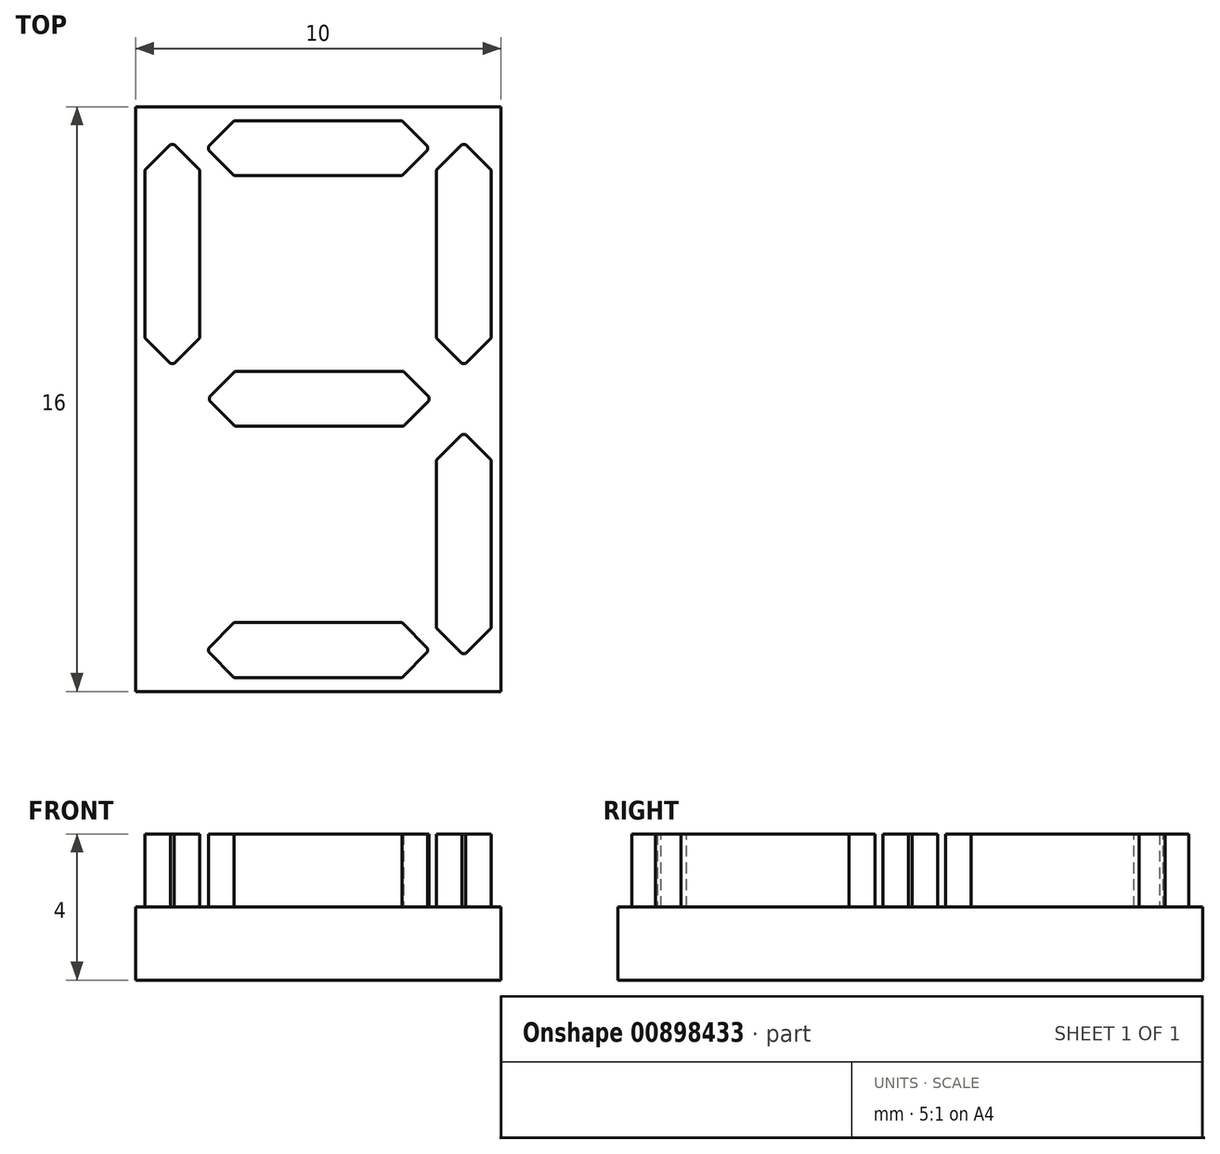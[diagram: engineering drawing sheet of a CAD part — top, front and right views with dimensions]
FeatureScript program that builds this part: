
annotation { "Feature Type Name" : "Feature", "Feature Type Description" : "" }
export const myFeature = defineFeature(function(context is Context, id is Id, definition is map)
    precondition{}
    {
        {
            var Q0;
            Q0=qCreatedBy(makeId("Top.planeOp"),FACE);
            var sketch = newSketch(context, id + "F0", { "sketchPlane" : qUnion([Q0])});
            skLineSegment(sketch, "E0.bottom", {"start": v(5, -8) * mm, "end": v(-5, -8) * mm});
            skLineSegment(sketch, "E0.top", {"start": v(5, 8) * mm, "end": v(-5, 8) * mm});
            skLineSegment(sketch, "E0.left", {"start": v(5, -8) * mm, "end": v(5, 8) * mm});
            skLineSegment(sketch, "E0.right", {"start": v(-5, -8) * mm, "end": v(-5, 8) * mm});
            skPoint(sketch, "E0.middle", {"position": v(0, 0) * mm});
            skSolve(sketch);
        }
        {
            var Q0;
            Q0=qSketchRegion(id+"F0",true);
            extrude(context, id + "F1", {"entities" : qUnion([Q0]), "oppositeDirection" : true, "depth" : 2 * mm, "offsetDistance" : 25 * mm});
        }
        {
            var Q0;
            Q0=makeQuery(id+"F1.opExtrude","CAP_FACE",FACE,{"disambiguationData":[OSD([sQuery(id+"F0.wireOp",EDGE,"E0.bottom"),sQuery(id+"F0.wireOp",EDGE,"E0.top"),sQuery(id+"F0.wireOp",EDGE,"E0.left"),sQuery(id+"F0.wireOp",EDGE,"E0.right")])],"isStart":true});
            var sketch = newSketch(context, id + "F2", { "sketchPlane" : qUnion([Q0])});
            skLineSegment(sketch, "E1", {"start": v(0, 8) * mm, "end": v(0, -8) * mm, "construction": true});
            skLineSegment(sketch, "E2", {"start": v(-5, 0) * mm, "end": v(5, 0) * mm, "construction": true});
            skLineSegment(sketch, "E3.bottom", {"start": v(3, 6.12) * mm, "end": v(-3, 6.12) * mm});
            skLineSegment(sketch, "E3.top", {"start": v(3, 7.62) * mm, "end": v(-3, 7.62) * mm});
            skLineSegment(sketch, "E3.left", {"start": v(3, 6.12) * mm, "end": v(3, 7.62) * mm});
            skLineSegment(sketch, "E3.right", {"start": v(-3, 6.12) * mm, "end": v(-3, 7.62) * mm});
            skPoint(sketch, "E3.middle", {"position": v(0, 6.87) * mm});
            skLineSegment(sketch, "E4.MirrorCS", {"start": v(-3, -6.12) * mm, "end": v(-3, -7.62) * mm});
            skLineSegment(sketch, "E5.MirrorCS", {"start": v(3, -6.12) * mm, "end": v(3, -7.62) * mm});
            skPoint(sketch, "E6.MirrorP", {"position": v(0, -6.87) * mm});
            skLineSegment(sketch, "E7.MirrorCS", {"start": v(3, -6.12) * mm, "end": v(-3, -6.12) * mm});
            skLineSegment(sketch, "E8.MirrorCS", {"start": v(4.74, -6.97) * mm, "end": v(4.74, -0.97) * mm});
            skLineSegment(sketch, "E9.MirrorCS", {"start": v(3, -7.62) * mm, "end": v(-3, -7.62) * mm});
            skLineSegment(sketch, "E10.MirrorCS", {"start": v(3.24, -6.97) * mm, "end": v(3.24, -0.47) * mm});
            skLineSegment(sketch, "E11.MirrorCS", {"start": v(3.24, -0.97) * mm, "end": v(4.74, -0.97) * mm});
            skLineSegment(sketch, "E12.MirrorCS", {"start": v(3.24, -6.97) * mm, "end": v(4.74, -6.97) * mm});
            skPoint(sketch, "E13.middle", {"position": v(0, 0) * mm});
            skLineSegment(sketch, "E14.MirrorCS", {"start": v(-3.24, 0.97) * mm, "end": v(-4.74, 0.97) * mm});
            skLineSegment(sketch, "E15.MirrorCS", {"start": v(4.74, 6.97) * mm, "end": v(4.74, 0.97) * mm});
            skLineSegment(sketch, "E16.MirrorCS", {"start": v(3.24, 0.97) * mm, "end": v(4.74, 0.97) * mm});
            skLineSegment(sketch, "E17.MirrorCS", {"start": v(3.24, 6.97) * mm, "end": v(4.74, 6.97) * mm});
            skLineSegment(sketch, "E18.MirrorCS", {"start": v(-4.74, 6.97) * mm, "end": v(-4.74, 0.97) * mm});
            skLineSegment(sketch, "E19.MirrorCS", {"start": v(3.24, 6.97) * mm, "end": v(3.24, 0.47) * mm});
            skLineSegment(sketch, "E20.MirrorCS", {"start": v(-3.24, 6.97) * mm, "end": v(-3.24, 0.47) * mm});
            skLineSegment(sketch, "E21.MirrorCS", {"start": v(-3.24, 6.97) * mm, "end": v(-4.74, 6.97) * mm});
            skLineSegment(sketch, "E22.MirrorCS", {"start": v(-2.97, 0.76) * mm, "end": v(-2.97, -0.74) * mm});
            skLineSegment(sketch, "E23.MirrorCS", {"start": v(3.03, 0.76) * mm, "end": v(3.03, -0.74) * mm});
            skLineSegment(sketch, "E24.MirrorCS", {"start": v(3.03, 0.76) * mm, "end": v(-2.97, 0.76) * mm});
            skLineSegment(sketch, "E25.MirrorCS", {"start": v(3.03, -0.74) * mm, "end": v(-2.97, -0.74) * mm});
            skSolve(sketch);
        }
        {
            var Q0;
            Q0=makeQuery(id+"F2.imprint","IMPRINT",FACE,{"disambiguationData":[TD([[makeQuery(id+"F2.imprint","IMPRINT",EDGE,{"derivedFrom":sQuery(id+"F2.wireOp",EDGE,"E14.MirrorCS")}),-1.0]])]});
            var Q1;
            Q1=makeQuery(id+"F2.imprint","IMPRINT",FACE,{"disambiguationData":[TD([[makeQuery(id+"F2.imprint","IMPRINT",EDGE,{"derivedFrom":sQuery(id+"F2.wireOp",EDGE,"E3.top")}),1.0]])]});
            var Q2;
            Q2=makeQuery(id+"F2.imprint","IMPRINT",FACE,{"disambiguationData":[TD([[makeQuery(id+"F2.imprint","IMPRINT",EDGE,{"derivedFrom":sQuery(id+"F2.wireOp",EDGE,"E15.MirrorCS")}),-1.0]])]});
            var Q3;
            Q3=makeQuery(id+"F2.imprint","IMPRINT",FACE,{"disambiguationData":[TD([[makeQuery(id+"F2.imprint","IMPRINT",EDGE,{"derivedFrom":sQuery(id+"F2.wireOp",EDGE,"E22.MirrorCS")}),1.0]])]});
            var Q4;
            Q4=makeQuery(id+"F2.imprint","IMPRINT",FACE,{"disambiguationData":[TD([[makeQuery(id+"F2.imprint","IMPRINT",EDGE,{"derivedFrom":sQuery(id+"F2.wireOp",EDGE,"8f7e5463-c989-4b34-adbd-07f48e1a05dd0.MirrorCS")}),-1.0]])]});
            var Q5;
            Q5=makeQuery(id+"F2.imprint","IMPRINT",FACE,{"disambiguationData":[TD([[makeQuery(id+"F2.imprint","IMPRINT",EDGE,{"derivedFrom":sQuery(id+"F2.wireOp",EDGE,"E4.MirrorCS")}),1.0]])]});
            var Q6;
            Q6=makeQuery(id+"F2.imprint","IMPRINT",FACE,{"disambiguationData":[TD([[makeQuery(id+"F2.imprint","IMPRINT",EDGE,{"derivedFrom":sQuery(id+"F2.wireOp",EDGE,"E8.MirrorCS")}),1.0]])]});
            extrude(context, id + "F3", {"entities" : qUnion([Q0, Q1, Q2, Q3, Q4, Q5, Q6]), "operationType" : NewBodyOperationType.ADD, "depth" : 2 * mm, "offsetDistance" : 25 * mm});
        }
        {
            var Q0;
            Q0=makeQuery(id+"F3.opExtrude","SWEPT_EDGE",EDGE,{"disambiguationData":[OSD([sQuery(id+"F2.wireOp",EDGE,"E3.left"),sQuery(id+"F2.wireOp",EDGE,"E3.bottom")])]});
            var Q1;
            Q1=makeQuery(id+"F3.opExtrude","SWEPT_EDGE",EDGE,{"disambiguationData":[OSD([sQuery(id+"F2.wireOp",EDGE,"E17.MirrorCS"),sQuery(id+"F2.wireOp",EDGE,"E19.MirrorCS")])]});
            var Q2;
            Q2=makeQuery(id+"F3.opExtrude","SWEPT_EDGE",EDGE,{"disambiguationData":[OSD([sQuery(id+"F2.wireOp",EDGE,"E16.MirrorCS"),sQuery(id+"F2.wireOp",EDGE,"E19.MirrorCS")])]});
            var Q3;
            Q3=makeQuery(id+"F3.opExtrude","SWEPT_EDGE",EDGE,{"disambiguationData":[OSD([sQuery(id+"F2.wireOp",EDGE,"E15.MirrorCS"),sQuery(id+"F2.wireOp",EDGE,"E16.MirrorCS")])]});
            var Q4;
            Q4=makeQuery(id+"F3.opExtrude","SWEPT_EDGE",EDGE,{"disambiguationData":[OSD([sQuery(id+"F2.wireOp",EDGE,"E10.MirrorCS"),sQuery(id+"F2.wireOp",EDGE,"E11.MirrorCS")])]});
            var Q5;
            Q5=makeQuery(id+"F3.opExtrude","SWEPT_EDGE",EDGE,{"disambiguationData":[OSD([sQuery(id+"F2.wireOp",EDGE,"E23.MirrorCS"),sQuery(id+"F2.wireOp",EDGE,"E25.MirrorCS")])]});
            var Q6;
            Q6=makeQuery(id+"F3.opExtrude","SWEPT_EDGE",EDGE,{"disambiguationData":[OSD([sQuery(id+"F2.wireOp",EDGE,"E22.MirrorCS"),sQuery(id+"F2.wireOp",EDGE,"E25.MirrorCS")])]});
            var Q7;
            Q7=makeQuery(id+"F3.opExtrude","SWEPT_EDGE",EDGE,{"disambiguationData":[OSD([sQuery(id+"F2.wireOp",EDGE,"E22.MirrorCS"),sQuery(id+"F2.wireOp",EDGE,"E24.MirrorCS")])]});
            var Q8;
            Q8=makeQuery(id+"F3.opExtrude","SWEPT_EDGE",EDGE,{"disambiguationData":[OSD([sQuery(id+"F2.wireOp",EDGE,"E14.MirrorCS"),sQuery(id+"F2.wireOp",EDGE,"E20.MirrorCS")])]});
            var Q9;
            Q9=makeQuery(id+"F3.opExtrude","SWEPT_EDGE",EDGE,{"disambiguationData":[OSD([sQuery(id+"F2.wireOp",EDGE,"E14.MirrorCS"),sQuery(id+"F2.wireOp",EDGE,"E18.MirrorCS")])]});
            var Q10;
            Q10=makeQuery(id+"F3.opExtrude","SWEPT_EDGE",EDGE,{"disambiguationData":[OSD([sQuery(id+"F2.wireOp",EDGE,"E18.MirrorCS"),sQuery(id+"F2.wireOp",EDGE,"E21.MirrorCS")])]});
            var Q11;
            Q11=makeQuery(id+"F3.opExtrude","SWEPT_EDGE",EDGE,{"disambiguationData":[OSD([sQuery(id+"F2.wireOp",EDGE,"E3.right"),sQuery(id+"F2.wireOp",EDGE,"E3.bottom")])]});
            var Q12;
            Q12=makeQuery(id+"F3.opExtrude","SWEPT_EDGE",EDGE,{"disambiguationData":[OSD([sQuery(id+"F2.wireOp",EDGE,"E3.top"),sQuery(id+"F2.wireOp",EDGE,"E3.right")])]});
            var Q13;
            Q13=makeQuery(id+"F3.opExtrude","SWEPT_EDGE",EDGE,{"disambiguationData":[OSD([sQuery(id+"F2.wireOp",EDGE,"E10.MirrorCS"),sQuery(id+"F2.wireOp",EDGE,"E12.MirrorCS")])]});
            var Q14;
            Q14=makeQuery(id+"F3.opExtrude","SWEPT_EDGE",EDGE,{"disambiguationData":[OSD([sQuery(id+"F2.wireOp",EDGE,"E8.MirrorCS"),sQuery(id+"F2.wireOp",EDGE,"E12.MirrorCS")])]});
            var Q15;
            Q15=makeQuery(id+"F3.opExtrude","SWEPT_EDGE",EDGE,{"disambiguationData":[OSD([sQuery(id+"F2.wireOp",EDGE,"E5.MirrorCS"),sQuery(id+"F2.wireOp",EDGE,"E9.MirrorCS")])]});
            var Q16;
            Q16=makeQuery(id+"F3.opExtrude","SWEPT_EDGE",EDGE,{"disambiguationData":[OSD([sQuery(id+"F2.wireOp",EDGE,"E4.MirrorCS"),sQuery(id+"F2.wireOp",EDGE,"E9.MirrorCS")])]});
            var Q17;
            Q17=makeQuery(id+"F3.opExtrude","SWEPT_EDGE",EDGE,{"disambiguationData":[OSD([sQuery(id+"F2.wireOp",EDGE,"8f7e5463-c989-4b34-adbd-07f48e1a05dd2.MirrorCS"),sQuery(id+"F2.wireOp",EDGE,"8f7e5463-c989-4b34-adbd-07f48e1a05dd3.MirrorCS")])]});
            var Q18;
            Q18=makeQuery(id+"F3.opExtrude","SWEPT_EDGE",EDGE,{"disambiguationData":[OSD([sQuery(id+"F2.wireOp",EDGE,"8f7e5463-c989-4b34-adbd-07f48e1a05dd0.MirrorCS"),sQuery(id+"F2.wireOp",EDGE,"8f7e5463-c989-4b34-adbd-07f48e1a05dd3.MirrorCS")])]});
            var Q19;
            Q19=makeQuery(id+"F3.opExtrude","SWEPT_EDGE",EDGE,{"disambiguationData":[OSD([sQuery(id+"F2.wireOp",EDGE,"E4.MirrorCS"),sQuery(id+"F2.wireOp",EDGE,"E7.MirrorCS")])]});
            var Q20;
            Q20=makeQuery(id+"F3.opExtrude","SWEPT_EDGE",EDGE,{"disambiguationData":[OSD([sQuery(id+"F2.wireOp",EDGE,"8f7e5463-c989-4b34-adbd-07f48e1a05dd0.MirrorCS"),sQuery(id+"F2.wireOp",EDGE,"8f7e5463-c989-4b34-adbd-07f48e1a05dd1.MirrorCS")])]});
            var Q21;
            Q21=makeQuery(id+"F3.opExtrude","SWEPT_EDGE",EDGE,{"disambiguationData":[OSD([sQuery(id+"F2.wireOp",EDGE,"8f7e5463-c989-4b34-adbd-07f48e1a05dd1.MirrorCS"),sQuery(id+"F2.wireOp",EDGE,"8f7e5463-c989-4b34-adbd-07f48e1a05dd2.MirrorCS")])]});
            var Q22;
            Q22=makeQuery(id+"F3.opExtrude","SWEPT_EDGE",EDGE,{"disambiguationData":[OSD([sQuery(id+"F2.wireOp",EDGE,"E23.MirrorCS"),sQuery(id+"F2.wireOp",EDGE,"E24.MirrorCS")])]});
            var Q23;
            Q23=makeQuery(id+"F3.opExtrude","SWEPT_EDGE",EDGE,{"disambiguationData":[OSD([sQuery(id+"F2.wireOp",EDGE,"E8.MirrorCS"),sQuery(id+"F2.wireOp",EDGE,"E11.MirrorCS")])]});
            var Q24;
            Q24=makeQuery(id+"F3.opExtrude","SWEPT_EDGE",EDGE,{"disambiguationData":[OSD([sQuery(id+"F2.wireOp",EDGE,"E5.MirrorCS"),sQuery(id+"F2.wireOp",EDGE,"E7.MirrorCS")])]});
            var Q25;
            Q25=makeQuery(id+"F3.opExtrude","SWEPT_EDGE",EDGE,{"disambiguationData":[OSD([sQuery(id+"F2.wireOp",EDGE,"E15.MirrorCS"),sQuery(id+"F2.wireOp",EDGE,"E17.MirrorCS")])]});
            var Q26;
            Q26=makeQuery(id+"F3.opExtrude","SWEPT_EDGE",EDGE,{"disambiguationData":[OSD([sQuery(id+"F2.wireOp",EDGE,"E3.top"),sQuery(id+"F2.wireOp",EDGE,"E3.left")])]});
            var Q27;
            Q27=makeQuery(id+"F3.opExtrude","SWEPT_EDGE",EDGE,{"disambiguationData":[OSD([sQuery(id+"F2.wireOp",EDGE,"E20.MirrorCS"),sQuery(id+"F2.wireOp",EDGE,"E21.MirrorCS")])]});
            chamfer(context, id + "F4", {"entities" : qUnion([Q0, Q1, Q2, Q3, Q4, Q5, Q6, Q7, Q8, Q9, Q10, Q11, Q12, Q13, Q14, Q15, Q16, Q17, Q18, Q19, Q20, Q21, Q22, Q23, Q24, Q25, Q26, Q27]), "width" : 0.7 * mm, "tangentPropagation" : true});
        }
    });
